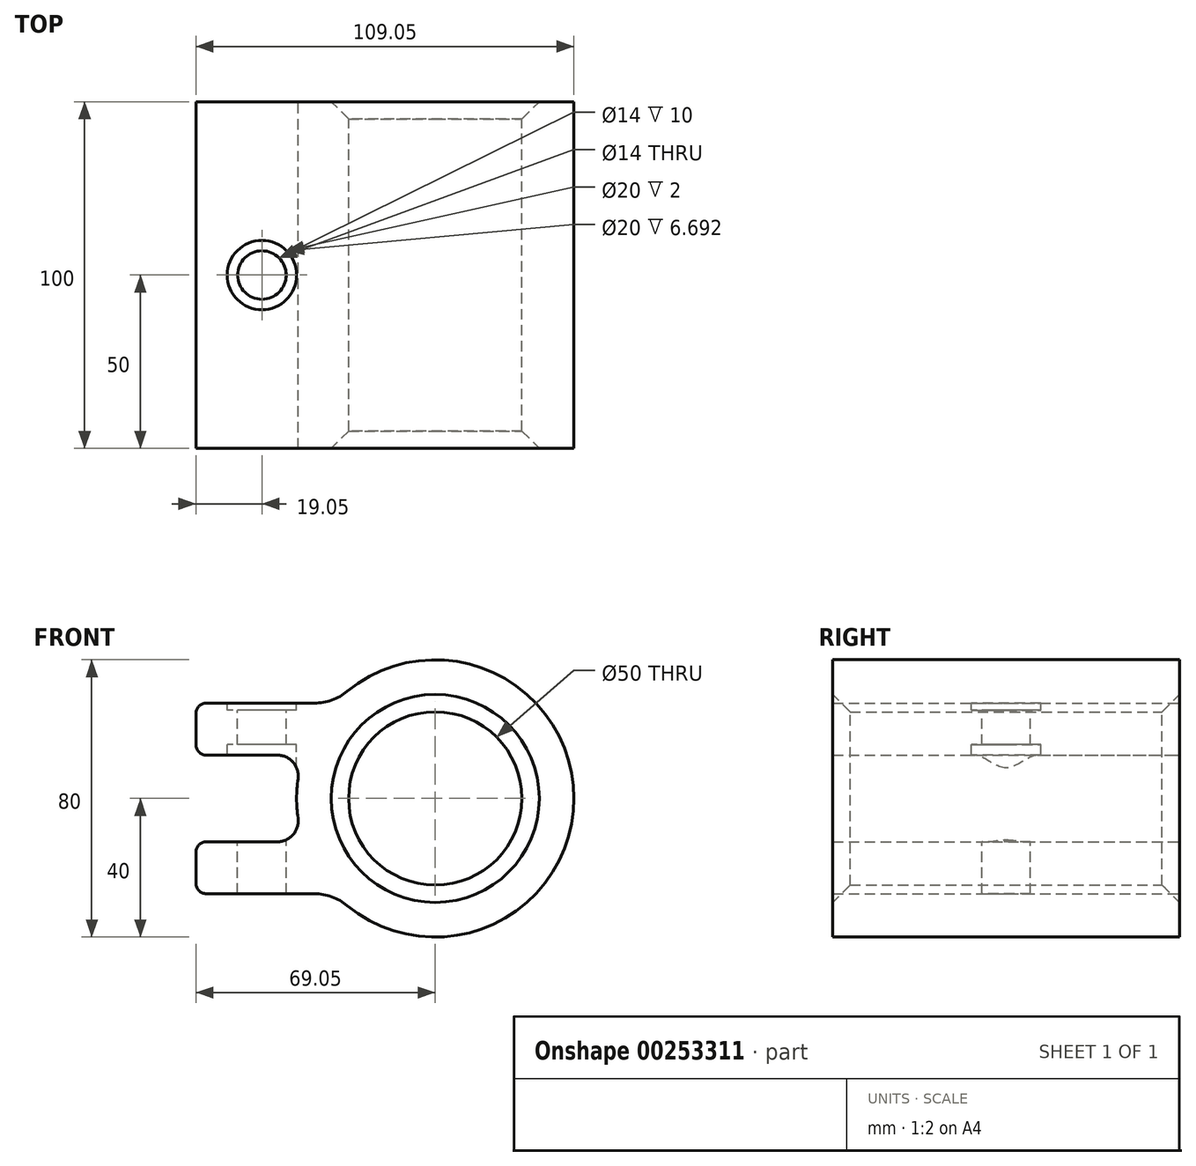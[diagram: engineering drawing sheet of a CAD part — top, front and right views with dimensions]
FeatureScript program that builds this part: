
annotation { "Feature Type Name" : "Feature", "Feature Type Description" : "" }
export const myFeature = defineFeature(function(context is Context, id is Id, definition is map)
    precondition{}
    {
        {
            var Q0;
            Q0=qCreatedBy(makeId("Front.planeOp"),FACE);
            var sketch = newSketch(context, id + "F0", { "sketchPlane" : qUnion([Q0])});
            skArc(sketch, "E0", {"start": v(-39.6, 5.65) * mm, "mid": v(-40, 0) * mm, "end": v(-39.6, -5.65) * mm});
            skLineSegment(sketch, "E1.bottom", {"start": v(-66.05, -12.5) * mm, "end": v(-45.54, -12.5) * mm});
            skLineSegment(sketch, "E1.top", {"start": v(-66.05, 12.5) * mm, "end": v(-45.54, 12.5) * mm});
            skLineSegment(sketch, "E2.bottom", {"start": v(-66.05, -27.5) * mm, "end": v(-34.91, -27.5) * mm});
            skLineSegment(sketch, "E2.top", {"start": v(-66.05, 27.5) * mm, "end": v(-34.91, 27.5) * mm});
            skLineSegment(sketch, "E2.left", {"start": v(-69.05, -24.5) * mm, "end": v(-69.05, -15.5) * mm});
            skPoint(sketch, "E2.right.start.orphan", {"position": v(69.05, -27.5) * mm});
            skPoint(sketch, "E3.orphan", {"position": v(69.05, 27.5) * mm});
            skPoint(sketch, "E4.orphan", {"position": v(69.05, 12.5) * mm});
            skPoint(sketch, "E5.orphan", {"position": v(69.05, -12.5) * mm});
            skLineSegment(sketch, "E6.trimOffspring", {"start": v(-69.05, 15.5) * mm, "end": v(-69.05, 24.5) * mm});
            skArc(sketch, "E7.trimOffspring", {"start": v(-25.39, -30.9) * mm, "mid": v(40, 0) * mm, "end": v(-25.39, 30.9) * mm});
            skPoint(sketch, "E8.visualSharp", {"position": v(-69.05, 27.5) * mm});
            skArc(sketch, "E8.filletArc", {"start": v(-66.05, 27.5) * mm, "mid": v(-68.17, 26.62) * mm, "end": v(-69.05, 24.5) * mm});
            skPoint(sketch, "E9.visualSharp", {"position": v(-69.05, 12.5) * mm});
            skArc(sketch, "E9.filletArc", {"start": v(-69.05, 15.5) * mm, "mid": v(-68.17, 13.38) * mm, "end": v(-66.05, 12.5) * mm});
            skPoint(sketch, "E10.visualSharp", {"position": v(-69.05, -12.5) * mm});
            skArc(sketch, "E10.filletArc", {"start": v(-66.05, -12.5) * mm, "mid": v(-68.17, -13.38) * mm, "end": v(-69.05, -15.5) * mm});
            skPoint(sketch, "E11.visualSharp", {"position": v(-69.05, -27.5) * mm});
            skArc(sketch, "E11.filletArc", {"start": v(-69.05, -24.5) * mm, "mid": v(-68.17, -26.62) * mm, "end": v(-66.05, -27.5) * mm});
            skPoint(sketch, "E12.visualSharp", {"position": v(-29.05, -27.5) * mm});
            skArc(sketch, "E12.filletArc", {"start": v(-25.39, -30.9) * mm, "mid": v(-29.85, -28.38) * mm, "end": v(-34.91, -27.5) * mm});
            skPoint(sketch, "E13.visualSharp", {"position": v(-29.05, 27.5) * mm});
            skArc(sketch, "E13.filletArc", {"start": v(-34.91, 27.5) * mm, "mid": v(-29.85, 28.38) * mm, "end": v(-25.39, 30.9) * mm});
            skCircle(sketch, "E14", {"center": v(0, 0) * mm, "radius": 25 * mm});
            skPoint(sketch, "E15.visualSharp", {"position": v(-38, 12.5) * mm});
            skArc(sketch, "E15.filletArc", {"start": v(-39.6, 5.65) * mm, "mid": v(-41, 10.43) * mm, "end": v(-45.54, 12.5) * mm});
            skPoint(sketch, "E16.visualSharp", {"position": v(-38, -12.5) * mm});
            skArc(sketch, "E16.filletArc", {"start": v(-45.54, -12.5) * mm, "mid": v(-41, -10.43) * mm, "end": v(-39.6, -5.65) * mm});
            skSolve(sketch);
        }
        {
            var Q0;
            Q0=makeQuery(id+"F0.imprint","IMPRINT",FACE,{"disambiguationData":[TD([[makeQuery(id+"F0.imprint","IMPRINT",EDGE,{"derivedFrom":sQuery(id+"F0.wireOp",EDGE,"E0")}),1.0]])]});
            extrude(context, id + "F1", {"entities" : qUnion([Q0]), "endBound" : BoundingType.SYMMETRIC, "depth" : 100 * mm});
        }
        {
            var Q0;
            Q0=makeQuery(id+"F1.opExtrude","CAP_EDGE",EDGE,{"disambiguationData":[OSD([sQuery(id+"F0.wireOp",EDGE,"E14")])],"isStart":false});
            var Q1;
            Q1=makeQuery(id+"F1.opExtrude","CAP_EDGE",EDGE,{"disambiguationData":[OSD([sQuery(id+"F0.wireOp",EDGE,"E14")])],"isStart":true});
            chamfer(context, id + "F2", {"entities" : qUnion([Q0, Q1]), "width" : 5 * mm, "tangentPropagation" : true});
        }
        {
            var Q0;
            Q0=makeQuery(id+"F1.opExtrude","SWEPT_FACE",FACE,{"disambiguationData":[OSD([sQuery(id+"F0.wireOp",EDGE,"E2.top")])]});
            var sketch = newSketch(context, id + "F3", { "sketchPlane" : qUnion([Q0])});
            skCircle(sketch, "E17", {"center": v(-50, 0) * mm, "radius": 10 * mm});
            skCircle(sketch, "E18", {"center": v(-50, 0) * mm, "radius": 7 * mm});
            skSolve(sketch);
        }
        {
            var Q0;
            Q0=makeQuery(id+"F3.imprint","IMPRINT",FACE,{"disambiguationData":[TD([[makeQuery(id+"F3.imprint","IMPRINT",EDGE,{"derivedFrom":sQuery(id+"F3.wireOp",EDGE,"E18")}),1.0]])]});
            extrude(context, id + "F4", {"entities" : qUnion([Q0]), "operationType" : NewBodyOperationType.REMOVE, "oppositeDirection" : true, "depth" : 80 * mm, "hasSecondDirection" : true, "secondDirectionOppositeDirection" : false, "secondDirectionDepth" : 25 * mm});
        }
        {
            var Q0;
            Q0=makeQuery(id+"F3.imprint","IMPRINT",FACE,{"disambiguationData":[TD([[makeQuery(id+"F3.imprint","IMPRINT",EDGE,{"derivedFrom":sQuery(id+"F3.wireOp",EDGE,"E17")}),1.0]])]});
            extrude(context, id + "F5", {"entities" : qUnion([Q0]), "operationType" : NewBodyOperationType.REMOVE, "oppositeDirection" : true, "depth" : 2 * mm});
        }
        {
            var Q0;
            Q0=makeQuery(id+"F3.imprint","IMPRINT",FACE,{"disambiguationData":[TD([[makeQuery(id+"F3.imprint","IMPRINT",EDGE,{"derivedFrom":sQuery(id+"F3.wireOp",EDGE,"E17")}),1.0]])]});
            extrude(context, id + "F6", {"entities" : qUnion([Q0]), "operationType" : NewBodyOperationType.REMOVE, "oppositeDirection" : true, "depth" : 20 * mm, "hasSecondDirection" : true, "secondDirectionOppositeDirection" : true, "secondDirectionDepth" : 12 * mm});
        }
    });
